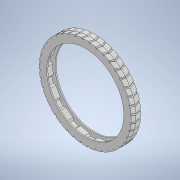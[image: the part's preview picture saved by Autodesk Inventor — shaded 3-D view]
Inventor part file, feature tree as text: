
AUTODESK INVENTOR PART (.ipt)
format: ipt  version: 2022 (Build 260153000, 153)  size: 1,056,768 bytes
history: native  units: mm
features: sketch x4, projected_geometry x4, other x3, extrude x2, plane x2, mirror x2, boolean_combine x1, loft x1, pattern_circular x1
ambient origin geometry x8: Origin, YZ Plane, XZ Plane, XY Plane, X Axis, Y Axis, Z Axis, Center Point
bodies: Solid2 (feature_tree), Solid3 (feature_tree), Solid1 (feature_tree)
feature tree (20):
  other  "Wheel.ipt"
  extrude  "Extrusion1"  Depth=10.0mm
  extrude  "Extrusion2"  Depth=1.0mm TaperAngle=0.0deg
  plane  "Work Plane1"
  mirror  "Mirror1"
  boolean_combine  "Combine1"
  sketch  "Sketch3"  dims[d5=1.0mm d6=0.0mm d7=0.2mm]
  plane  "Work Plane2"
  sketch  "Sketch4"  dims[d8=1.0mm d9=30.0deg d10=30.0deg d11=5.0mm d12=1.0mm d13=5.0mm d14=30.0deg d15=30.0deg d16=0.349066mm d17=0.0mm d18=90.0deg d19=0.0mm d20=90.0deg d21=400.0mm d22=360.0deg]
  loft  "Loft1"
  mirror  "Mirror2"
  pattern_circular  "Circular Pattern1"  Angle=30.0deg  [1 undecoded]
  other  "Solid2::Wheel.ipt"
  other  "TaggingFeature1"
  sketch  "Sketch1"  dims[d0=10.0mm d1=2.0mm]
  projected_geometry  "Projected Loop1"
  sketch  "Sketch2"  dims[d2=2.0mm d3=1.0mm d4=0.0mm]
  projected_geometry  "Projected Loop2"
  projected_geometry  "Projected Loop3"
  projected_geometry  "Projected Loop4"
note: 1 required parameter value undecoded (feature->parameter linkage not recoverable at this tier; creation-order binding heuristic only, values carry confidence <= 0.55)
